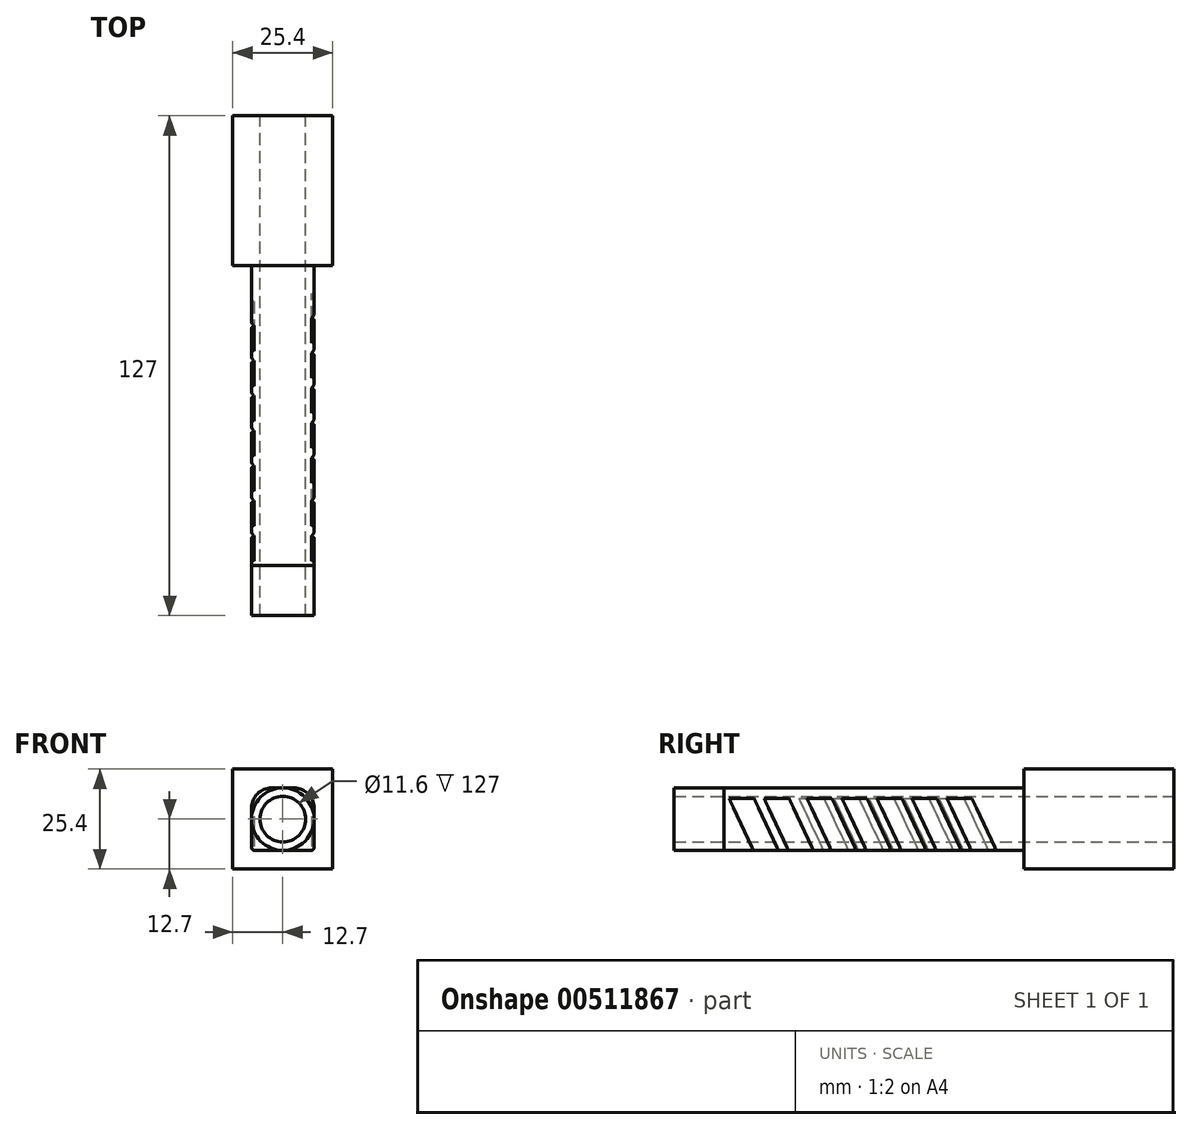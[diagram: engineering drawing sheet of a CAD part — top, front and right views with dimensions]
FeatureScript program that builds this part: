
annotation { "Feature Type Name" : "Feature", "Feature Type Description" : "" }
export const myFeature = defineFeature(function(context is Context, id is Id, definition is map)
    precondition{}
    {
        {
            var Q0;
            Q0=qCreatedBy(makeId("Front.planeOp"),FACE);
            var sketch = newSketch(context, id + "F0", { "sketchPlane" : qUnion([Q0])});
            skLineSegment(sketch, "E0.bottom", {"start": v(12.7, -12.7) * mm, "end": v(-12.7, -12.7) * mm});
            skLineSegment(sketch, "E0.top", {"start": v(12.7, 12.7) * mm, "end": v(-12.7, 12.7) * mm});
            skLineSegment(sketch, "E0.left", {"start": v(12.7, -12.7) * mm, "end": v(12.7, 12.7) * mm});
            skLineSegment(sketch, "E0.right", {"start": v(-12.7, -12.7) * mm, "end": v(-12.7, 12.7) * mm});
            skPoint(sketch, "E0.middle", {"position": v(0, 0) * mm});
            skCircle(sketch, "E1", {"center": v(0, 0) * mm, "radius": 7.94 * mm});
            skCircle(sketch, "E2", {"center": v(0, 0) * mm, "radius": 5.8 * mm});
            skLineSegment(sketch, "E3.bottom", {"start": v(-7.94, -7.94) * mm, "end": v(7.94, -7.94) * mm});
            skLineSegment(sketch, "E3.top", {"start": v(-7.94, 7.94) * mm, "end": v(7.94, 7.94) * mm});
            skLineSegment(sketch, "E3.left", {"start": v(-7.94, -7.94) * mm, "end": v(-7.94, 7.94) * mm});
            skLineSegment(sketch, "E3.right", {"start": v(7.94, -7.94) * mm, "end": v(7.94, 7.94) * mm});
            skSolve(sketch);
        }
        {
            var Q0;
            Q0=qSketchRegion(id+"F0",true);
            var Q1;
            Q1=makeQuery(id+"F0.imprint","IMPRINT",FACE,{"disambiguationData":[TD([[makeQuery(id+"F0.imprint","IMPRINT",EDGE,{"derivedFrom":sQuery(id+"F0.wireOp",EDGE,"E1")}),1.0]])]});
            extrude(context, id + "F1", {"entities" : qUnion([Q0, Q1]), "depth" : 38.1 * mm});
        }
        {
            var Q0;
            Q0=makeQuery(id+"F0.imprint","IMPRINT",FACE,{"disambiguationData":[TD([[makeQuery(id+"F0.imprint","IMPRINT",EDGE,{"derivedFrom":sQuery(id+"F0.wireOp",EDGE,"E1")}),1.0]])]});
            extrude(context, id + "F2", {"entities" : qUnion([Q0]), "operationType" : NewBodyOperationType.ADD, "depth" : 127 * mm, "offsetDistance" : 25.4 * mm});
        }
        {
            var Q0;
            {var subQ0=sQuery(id+"F0.wireOp",EDGE,"E3.right");var subQ1=sQuery(id+"F0.wireOp",EDGE,"E1");var subQ2=makeQuery(id+"F0.imprint","INTERSECT",VERTEX,{"derivedFrom":[subQ1,subQ0]});Q0=makeQuery(id+"F0.imprint","IMPRINT",FACE,{"disambiguationData":[TD([[makeQuery(id+"F0.imprint","IMPRINT",EDGE,{"disambiguationData":[TD([[subQ2,1.0]])],"derivedFrom":subQ1}),-1.0]])]});}
            var Q1;
            {var subQ0=sQuery(id+"F0.wireOp",EDGE,"E3.top");var subQ1=sQuery(id+"F0.wireOp",EDGE,"E1");var subQ2=makeQuery(id+"F0.imprint","INTERSECT",VERTEX,{"derivedFrom":[subQ1,subQ0]});Q1=makeQuery(id+"F0.imprint","IMPRINT",FACE,{"disambiguationData":[TD([[makeQuery(id+"F0.imprint","IMPRINT",EDGE,{"disambiguationData":[TD([[subQ2,1.0]])],"derivedFrom":subQ1}),-1.0]])]});}
            var Q2;
            {var subQ0=sQuery(id+"F0.wireOp",EDGE,"E3.top");var subQ1=sQuery(id+"F0.wireOp",EDGE,"E1");var subQ2=makeQuery(id+"F0.imprint","INTERSECT",VERTEX,{"derivedFrom":[subQ1,subQ0]});Q2=makeQuery(id+"F0.imprint","IMPRINT",FACE,{"disambiguationData":[TD([[makeQuery(id+"F0.imprint","IMPRINT",EDGE,{"disambiguationData":[TD([[subQ2,-1.0]])],"derivedFrom":subQ1}),-1.0]])]});}
            var Q3;
            {var subQ0=sQuery(id+"F0.wireOp",EDGE,"E3.left");var subQ1=sQuery(id+"F0.wireOp",EDGE,"E1");var subQ2=makeQuery(id+"F0.imprint","INTERSECT",VERTEX,{"derivedFrom":[subQ1,subQ0]});Q3=makeQuery(id+"F0.imprint","IMPRINT",FACE,{"disambiguationData":[TD([[makeQuery(id+"F0.imprint","IMPRINT",EDGE,{"disambiguationData":[TD([[subQ2,-1.0]])],"derivedFrom":subQ1}),-1.0]])]});}
            extrude(context, id + "F3", {"entities" : qUnion([Q0, Q1, Q2, Q3]), "operationType" : NewBodyOperationType.ADD, "depth" : 127 * mm, "offsetDistance" : 25.4 * mm});
        }
        {
            var Q0;
            {var subQ0=sQuery(id+"F0.wireOp",EDGE,"E3.left");Q0=makeQuery(id+"F3.boolean.opBoolean","MERGE",FACE,{"derivedFrom":[makeQuery(id+"F3.opExtrude","SWEPT_FACE",FACE,{"disambiguationData":[OSD([subQ0]),TDD([makeQuery(id+"F0.imprint","IMPRINT",EDGE,{"disambiguationData":[TD([[makeQuery(id+"F0.imprint","INTERSECT",VERTEX,{"derivedFrom":[sQuery(id+"F0.wireOp",EDGE,"E3.bottom"),subQ0]}),-1.0]])],"derivedFrom":subQ0})])]}),makeQuery(id+"F3.opExtrude","SWEPT_FACE",FACE,{"disambiguationData":[OSD([subQ0]),TDD([makeQuery(id+"F0.imprint","IMPRINT",EDGE,{"disambiguationData":[TD([[makeQuery(id+"F0.imprint","INTERSECT",VERTEX,{"derivedFrom":[sQuery(id+"F0.wireOp",EDGE,"E3.top"),subQ0]}),1.0]])],"derivedFrom":subQ0})])]})]});}
            var sketch = newSketch(context, id + "F4", { "sketchPlane" : qUnion([Q0])});
            skLineSegment(sketch, "E4", {"start": v(127, 7.94) * mm, "end": v(114.3, 7.94) * mm});
            skLineSegment(sketch, "E5", {"start": v(114.3, 7.94) * mm, "end": v(106.9, -7.94) * mm});
            skLineSegment(sketch, "E6", {"start": v(114.3, 7.94) * mm, "end": v(107.95, 7.94) * mm});
            skLineSegment(sketch, "E7", {"start": v(107.95, 7.94) * mm, "end": v(100.55, -7.94) * mm});
            skLineSegment(sketch, "E8", {"start": v(100.55, -7.94) * mm, "end": v(106.9, -7.94) * mm});
            skLineSegment(sketch, "E9", {"start": v(105.4, 7.94) * mm, "end": v(98, -7.94) * mm});
            skLineSegment(sketch, "E10", {"start": v(105.4, 7.94) * mm, "end": v(99.06, 7.94) * mm});
            skLineSegment(sketch, "E11", {"start": v(99.06, 7.94) * mm, "end": v(91.66, -7.94) * mm});
            skLineSegment(sketch, "E12", {"start": v(91.66, -7.94) * mm, "end": v(98, -7.94) * mm});
            skLineSegment(sketch, "E13", {"start": v(96.52, 7.94) * mm, "end": v(89.12, -7.94) * mm});
            skLineSegment(sketch, "E14", {"start": v(96.52, 7.94) * mm, "end": v(90.17, 7.94) * mm});
            skLineSegment(sketch, "E15", {"start": v(90.17, 7.94) * mm, "end": v(82.77, -7.94) * mm});
            skLineSegment(sketch, "E16", {"start": v(82.77, -7.94) * mm, "end": v(89.12, -7.94) * mm});
            skLineSegment(sketch, "E17", {"start": v(87.63, 7.94) * mm, "end": v(80.23, -7.94) * mm});
            skLineSegment(sketch, "E18", {"start": v(87.63, 7.94) * mm, "end": v(81.28, 7.94) * mm});
            skLineSegment(sketch, "E19", {"start": v(81.28, 7.94) * mm, "end": v(73.88, -7.94) * mm});
            skLineSegment(sketch, "E20", {"start": v(73.88, -7.94) * mm, "end": v(80.23, -7.94) * mm});
            skLineSegment(sketch, "E21", {"start": v(78.74, 7.94) * mm, "end": v(71.34, -7.94) * mm});
            skLineSegment(sketch, "E22", {"start": v(78.74, 7.94) * mm, "end": v(72.4, 7.94) * mm});
            skLineSegment(sketch, "E23", {"start": v(72.4, 7.94) * mm, "end": v(64.99, -7.94) * mm});
            skLineSegment(sketch, "E24", {"start": v(64.99, -7.94) * mm, "end": v(71.34, -7.94) * mm});
            skLineSegment(sketch, "E25", {"start": v(69.85, 7.94) * mm, "end": v(62.45, -7.94) * mm});
            skLineSegment(sketch, "E26", {"start": v(69.85, 7.94) * mm, "end": v(63.5, 7.94) * mm});
            skLineSegment(sketch, "E27", {"start": v(63.5, 7.94) * mm, "end": v(56.1, -7.94) * mm});
            skLineSegment(sketch, "E28", {"start": v(56.1, -7.94) * mm, "end": v(62.45, -7.94) * mm});
            skLineSegment(sketch, "E29", {"start": v(60.96, 7.94) * mm, "end": v(53.56, -7.94) * mm});
            skLineSegment(sketch, "E30", {"start": v(60.96, 7.94) * mm, "end": v(54.61, 7.94) * mm});
            skLineSegment(sketch, "E31", {"start": v(54.61, 7.94) * mm, "end": v(47.2, -7.94) * mm});
            skLineSegment(sketch, "E32", {"start": v(47.2, -7.94) * mm, "end": v(53.56, -7.94) * mm});
            skSolve(sketch);
        }
        {
            var Q0;
            Q0 = qSketchRegion(id + "F4", true);
            extrude(context, id + "F5", {"entities" : qUnion([Q0]), "operationType" : NewBodyOperationType.REMOVE, "oppositeDirection" : true, "depth" : 0.64 * mm, "offsetDistance" : 25.4 * mm});
        }
        {
            var Q0;
            {var subQ0=sQuery(id+"F0.wireOp",EDGE,"E3.right");Q0=makeQuery(id+"F3.boolean.opBoolean","MERGE",FACE,{"derivedFrom":[makeQuery(id+"F3.opExtrude","SWEPT_FACE",FACE,{"disambiguationData":[OSD([subQ0]),TDD([makeQuery(id+"F0.imprint","IMPRINT",EDGE,{"disambiguationData":[TD([[makeQuery(id+"F0.imprint","INTERSECT",VERTEX,{"derivedFrom":[sQuery(id+"F0.wireOp",EDGE,"E3.bottom"),subQ0]}),-1.0]])],"derivedFrom":subQ0})])]}),makeQuery(id+"F3.opExtrude","SWEPT_FACE",FACE,{"disambiguationData":[OSD([subQ0]),TDD([makeQuery(id+"F0.imprint","IMPRINT",EDGE,{"disambiguationData":[TD([[makeQuery(id+"F0.imprint","INTERSECT",VERTEX,{"derivedFrom":[sQuery(id+"F0.wireOp",EDGE,"E3.top"),subQ0]}),1.0]])],"derivedFrom":subQ0})])]})]});}
            var sketch = newSketch(context, id + "F6", { "sketchPlane" : qUnion([Q0])});
            skLineSegment(sketch, "E33", {"start": v(-127, 7.94) * mm, "end": v(-114.3, 7.94) * mm});
            skLineSegment(sketch, "E34", {"start": v(-114.3, 7.94) * mm, "end": v(-106.9, -7.94) * mm});
            skLineSegment(sketch, "E35", {"start": v(-106.9, -7.94) * mm, "end": v(-100.55, -7.94) * mm});
            skLineSegment(sketch, "E36", {"start": v(-100.55, -7.94) * mm, "end": v(-107.95, 7.94) * mm});
            skLineSegment(sketch, "E37", {"start": v(-107.95, 7.94) * mm, "end": v(-114.3, 7.94) * mm});
            skLineSegment(sketch, "E38", {"start": v(-105.41, 7.94) * mm, "end": v(-98, -7.94) * mm});
            skLineSegment(sketch, "E39", {"start": v(-98, -7.94) * mm, "end": v(-91.66, -7.94) * mm});
            skLineSegment(sketch, "E40", {"start": v(-91.66, -7.94) * mm, "end": v(-99.06, 7.94) * mm});
            skLineSegment(sketch, "E41", {"start": v(-99.06, 7.94) * mm, "end": v(-105.4, 7.94) * mm});
            skLineSegment(sketch, "E42", {"start": v(-94.53, 7.94) * mm, "end": v(-87.13, -7.94) * mm});
            skLineSegment(sketch, "E43", {"start": v(-87.13, -7.94) * mm, "end": v(-80.78, -7.94) * mm});
            skLineSegment(sketch, "E44", {"start": v(-80.78, -7.94) * mm, "end": v(-88.18, 7.94) * mm});
            skLineSegment(sketch, "E45", {"start": v(-88.18, 7.94) * mm, "end": v(-96.52, 7.94) * mm});
            skLineSegment(sketch, "E46", {"start": v(-85.64, 7.94) * mm, "end": v(-78.24, -7.94) * mm});
            skLineSegment(sketch, "E47", {"start": v(-78.24, -7.94) * mm, "end": v(-71.89, -7.94) * mm});
            skLineSegment(sketch, "E48", {"start": v(-71.89, -7.94) * mm, "end": v(-79.29, 7.94) * mm});
            skLineSegment(sketch, "E49", {"start": v(-79.29, 7.94) * mm, "end": v(-85.64, 7.94) * mm});
            skLineSegment(sketch, "E50", {"start": v(-76.75, 7.94) * mm, "end": v(-69.35, -7.94) * mm});
            skLineSegment(sketch, "E51", {"start": v(-69.35, -7.94) * mm, "end": v(-63, -7.94) * mm});
            skLineSegment(sketch, "E52", {"start": v(-63, -7.94) * mm, "end": v(-70.4, 7.94) * mm});
            skLineSegment(sketch, "E53", {"start": v(-67.86, 7.94) * mm, "end": v(-60.46, -7.94) * mm});
            skLineSegment(sketch, "E54", {"start": v(-60.46, -7.94) * mm, "end": v(-54.1, -7.94) * mm});
            skLineSegment(sketch, "E55", {"start": v(-54.1, -7.94) * mm, "end": v(-61.5, 7.94) * mm});
            skLineSegment(sketch, "E56", {"start": v(-61.5, 7.94) * mm, "end": v(-67.86, 7.94) * mm});
            skLineSegment(sketch, "E57", {"start": v(-76.75, 7.94) * mm, "end": v(-70.4, 7.94) * mm});
            skLineSegment(sketch, "E58", {"start": v(-61.5, 7.94) * mm, "end": v(-58.97, 7.94) * mm});
            skLineSegment(sketch, "E59", {"start": v(-58.97, 7.94) * mm, "end": v(-51.57, -7.94) * mm});
            skLineSegment(sketch, "E60", {"start": v(-51.57, -7.94) * mm, "end": v(-45.22, -7.94) * mm});
            skLineSegment(sketch, "E61", {"start": v(-45.22, -7.94) * mm, "end": v(-52.62, 7.94) * mm});
            skLineSegment(sketch, "E62", {"start": v(-58.97, 7.94) * mm, "end": v(-52.62, 7.94) * mm});
            skSolve(sketch);
        }
        {
            var Q0;
            Q0 = qSketchRegion(id + "F6", true);
            extrude(context, id + "F7", {"entities" : qUnion([Q0]), "operationType" : NewBodyOperationType.REMOVE, "oppositeDirection" : true, "depth" : 0.64 * mm, "offsetDistance" : 25.4 * mm});
        }
        {
            var Q0;
            {var subQ0=sQuery(id+"F0.wireOp",EDGE,"E3.right");var subQ1=sQuery(id+"F0.wireOp",EDGE,"E3.top");Q0=makeQuery(id+"F7.boolean.opBoolean","SPLIT",EDGE,{"disambiguationData":[TD([makeQuery(id+"F7.opExtrude","SWEPT_FACE",FACE,{"disambiguationData":[OSD([sQuery(id+"F6.wireOp",EDGE,"E44")])]})])],"derivedFrom":makeQuery(id+"F3.opExtrude","SWEPT_EDGE",EDGE,{"disambiguationData":[OSD([subQ1,subQ0])]})});}
            var Q1;
            {var subQ0=sQuery(id+"F0.wireOp",EDGE,"E3.left");var subQ3=sQuery(id+"F0.wireOp",EDGE,"E3.top");Q1=makeQuery(id+"F5.boolean.opBoolean","SPLIT",EDGE,{"disambiguationData":[TD([makeQuery(id+"F5.opExtrude","SWEPT_FACE",FACE,{"disambiguationData":[OSD([sQuery(id+"F4.wireOp",EDGE,"E5")])]})])],"derivedFrom":makeQuery(id+"F3.opExtrude","SWEPT_EDGE",EDGE,{"disambiguationData":[OSD([subQ3,subQ0])]})});}
            fillet(context, id + "F8", {"entities" : qUnion([Q0, Q1]), "radius" : 5.08 * mm, "tangentPropagation" : true, "allowEdgeOverflow" : false});
        }
        {
            var Q0;
            {var subQ0=sQuery(id+"F0.wireOp",EDGE,"E3.left");var subQ1=sQuery(id+"F0.wireOp",EDGE,"E3.bottom");Q0=makeQuery(id+"F5.boolean.opBoolean","SPLIT",EDGE,{"disambiguationData":[TD([makeQuery(id+"F5.opExtrude","SWEPT_FACE",FACE,{"disambiguationData":[OSD([sQuery(id+"F4.wireOp",EDGE,"E5")])]})])],"derivedFrom":makeQuery(id+"F3.opExtrude","SWEPT_EDGE",EDGE,{"disambiguationData":[OSD([subQ1,subQ0])]})});}
            var Q1;
            {var subQ1=sQuery(id+"F0.wireOp",EDGE,"E3.bottom");var subQ3=sQuery(id+"F0.wireOp",EDGE,"E3.right");Q1=makeQuery(id+"F7.boolean.opBoolean","SPLIT",EDGE,{"disambiguationData":[TD([makeQuery(id+"F7.opExtrude","SWEPT_FACE",FACE,{"disambiguationData":[OSD([sQuery(id+"F6.wireOp",EDGE,"E34")])]})])],"derivedFrom":makeQuery(id+"F3.opExtrude","SWEPT_EDGE",EDGE,{"disambiguationData":[OSD([subQ1,subQ3])]})});}
            fillet(context, id + "F9", {"entities" : qUnion([Q0, Q1]), "radius" : 0.76 * mm, "tangentPropagation" : true, "allowEdgeOverflow" : false});
        }
        {
            var Q0;
            {var subQ0=sQuery(id+"F0.wireOp",EDGE,"E3.right");var subQ1=sQuery(id+"F0.wireOp",EDGE,"E3.bottom");var subQ2=sQuery(id+"F0.wireOp",EDGE,"E1");var subQ3=sQuery(id+"F0.wireOp",EDGE,"E3.left");var subQ4=sQuery(id+"F0.wireOp",EDGE,"E3.top");Q0=makeQuery(id+"F3.boolean.opBoolean","MERGE",FACE,{"derivedFrom":[makeQuery(id+"F2.opExtrude","CAP_FACE",FACE,{"disambiguationData":[OSD([subQ2,sQuery(id+"F0.wireOp",EDGE,"E2")])],"isStart":false}),makeQuery(id+"F3.opExtrude","CAP_FACE",FACE,{"disambiguationData":[OSD([subQ2,subQ4,subQ0])],"isStart":false}),makeQuery(id+"F3.opExtrude","CAP_FACE",FACE,{"disambiguationData":[OSD([subQ2,subQ4,subQ3])],"isStart":false}),makeQuery(id+"F3.opExtrude","CAP_FACE",FACE,{"disambiguationData":[OSD([subQ2,subQ1,subQ3])],"isStart":false}),makeQuery(id+"F3.opExtrude","CAP_FACE",FACE,{"disambiguationData":[OSD([subQ2,subQ1,subQ0])],"isStart":false})]});}
            var sketch = newSketch(context, id + "F10", { "sketchPlane" : qUnion([Q0])});
            skCircle(sketch, "E63", {"center": v(0, 0) * mm, "radius": 7.94 * mm});
            skCircle(sketch, "E64", {"center": v(0, 0) * mm, "radius": 11.53 * mm});
            skSolve(sketch);
        }
        {
            var Q0;
            Q0 = qSketchRegion(id + "F10", true);
            extrude(context, id + "F11", {"entities" : qUnion([Q0]), "operationType" : NewBodyOperationType.REMOVE, "oppositeDirection" : true, "depth" : 12.7 * mm, "offsetDistance" : 25.4 * mm});
        }
    });
